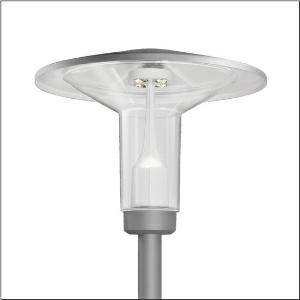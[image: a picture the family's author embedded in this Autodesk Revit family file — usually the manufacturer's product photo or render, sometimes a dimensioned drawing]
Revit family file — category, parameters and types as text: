
# Revit family: laterne_iq___st1_2a_5xa5255ef14h_6af0
name_source: partatom
category: Lighting Fixtures
units: mm (PartAtom-declared; Revit-internal decimal feet)

## family parameters
Cut with Voids When Loaded = No
Host = Face
Light Source = No
Part Type = Normal
Room Calculation Point = No
Round Connector Dimension = Use Diameter
Shared = No

## types (1)
- --- (1 x LED, 1540 lm, 10.5 W, 3000K)
    Apparent Load = 11 VA
    CIE Flux Codes = 25 63 94 98 100
    Color Rendering = 70
    Color Temperature = 3000K
    Default Elevation = 1800 mm
    Description = Lantern iQ, mast luminaire, Module 540 iQ-SR, primary light control with 3 zone facetted reflector, of plastic, silver coated, highly specular, structured, primary optical cover: cover, of PMMA, transparent, light distribution: ST1.2a, light emission: direct distribution, primary light characteristic: asymmetric, installation type: post-top, LED, High Power LED, rated luminous flux: 1.540lm, luminous efficacy: 147lm/W, light colour: 730, colour temperature: 3000K, control gear: ECG iQ, control: Auto-Match, Temp-Guard, Lumen-Switch, Night-Set, Smart-Wire, Light-Fading, Desk-Remote (wireless, voltage-free reading and setting of iQ features in the workshop via application-optimized NFC function/RFID function), optimised constant luminous flux control (CLO 2.0), Street-Remote, pre-setting: logarithmic dimming characteristic, with terminal, 6-pole, max. 2.5mm², mains connection: 230..240V, AC, 50/60Hz, start of lifetime: 11W, end of service life: 11W, reduction: 5W, luminaire housing, upper part, of glass-fibre reinforced polyester, coated, Siteco® metallic grey (DB 702S), diameter: 750mm, height: 583mm, spigot size: d x l = 76 x 70mm (post-top) | with reducer (optional accessory) 60 x 70mm, post-top mast mounting element, of diecast aluminium, coated, Siteco® metallic grey (DB 702S), Module 540 iQ-SR, traffic white (RAL 9016), equipment: standard, protection rating (complete): IP65, insulation class (complete): insulation class II (safety insulation), certification: CE, ENEC, VDE, packaging unit: 1 piece

Light Distribution: ST1.2a
    Height = 583 mm
    Lamp = 1 x LED
    Lamp Light Flux = 1540 lm
    Lamp Power = 10.5 W
    Lamp count = 1
    Length = 750 mm
    Luminous efficacy = 147 lm/W
    Manufacturer = Siteco
    ModVariant = No
    Model = 5XA5255EF14H
    Number of Poles = 1
    OnlyDefault = Yes
    Power Factor = 1
    Product Name = Laterne iQ | ST1.2a
    Product group = mast luminaire | pylon top
    ProductGroupID = 6100
    Protection Class = Protection class II
    Protection Degree = IP 65
    RLX_Detail_Level = 1
    RLX_Emergency_Light_Flux = 0 lm
    RLX_Emergency_Type = 0
    RLX_Emergency_Type_DB = No
    RlxData = <blob elided: 103365 chars, md5=ebbc6530>
    Socket = socket
    Standby Power = 0 W
    System Light Flux = 1540 lm
    System Power = 11 W
    Type Comments = factory setting: luminous flux: 100 % | dim-lin: 254 | 419 mA
    Type Image = l_1006050.jpg
    URL = http://relux.com
    VarID = @adj_130993
    Voltage = 0 V
    Weight = 0.00 kg
    Width = 0 mm  [stored 0 ft]

note: [stored X ft] marks values corroborated as IEEE doubles in the binary element streams (Revit-internal decimal feet)

## geometry (parser evidence)
native form markers: Blend x4, Sweep x9
no freeform markers — native parametric forms only
